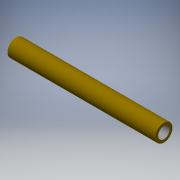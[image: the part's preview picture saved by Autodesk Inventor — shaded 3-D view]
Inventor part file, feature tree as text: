
AUTODESK INVENTOR PART (.ipt)
format: ipt  version: 2016 (Build 200138000, 138)  size: 94,208 bytes
history: native  units: mm
features: extrude x2, sketch x2
ambient origin geometry x8: Origin, YZ Plane, XZ Plane, XY Plane, X Axis, Y Axis, Z Axis, Center Point
bodies: Solid1 (feature_tree)
feature tree (4):
  extrude  "Extrusion1"  Depth=77.0mm TaperAngle=0.0deg
  extrude  "Extrusion2"  Depth=15.0mm TaperAngle=0.0deg
  sketch  "Sketch1"  dims[d0=9.0mm d1=77.0mm d2=0.0mm]
  sketch  "Sketch2"  dims[d3=6.0mm d4=15.0mm d5=0.0mm]
